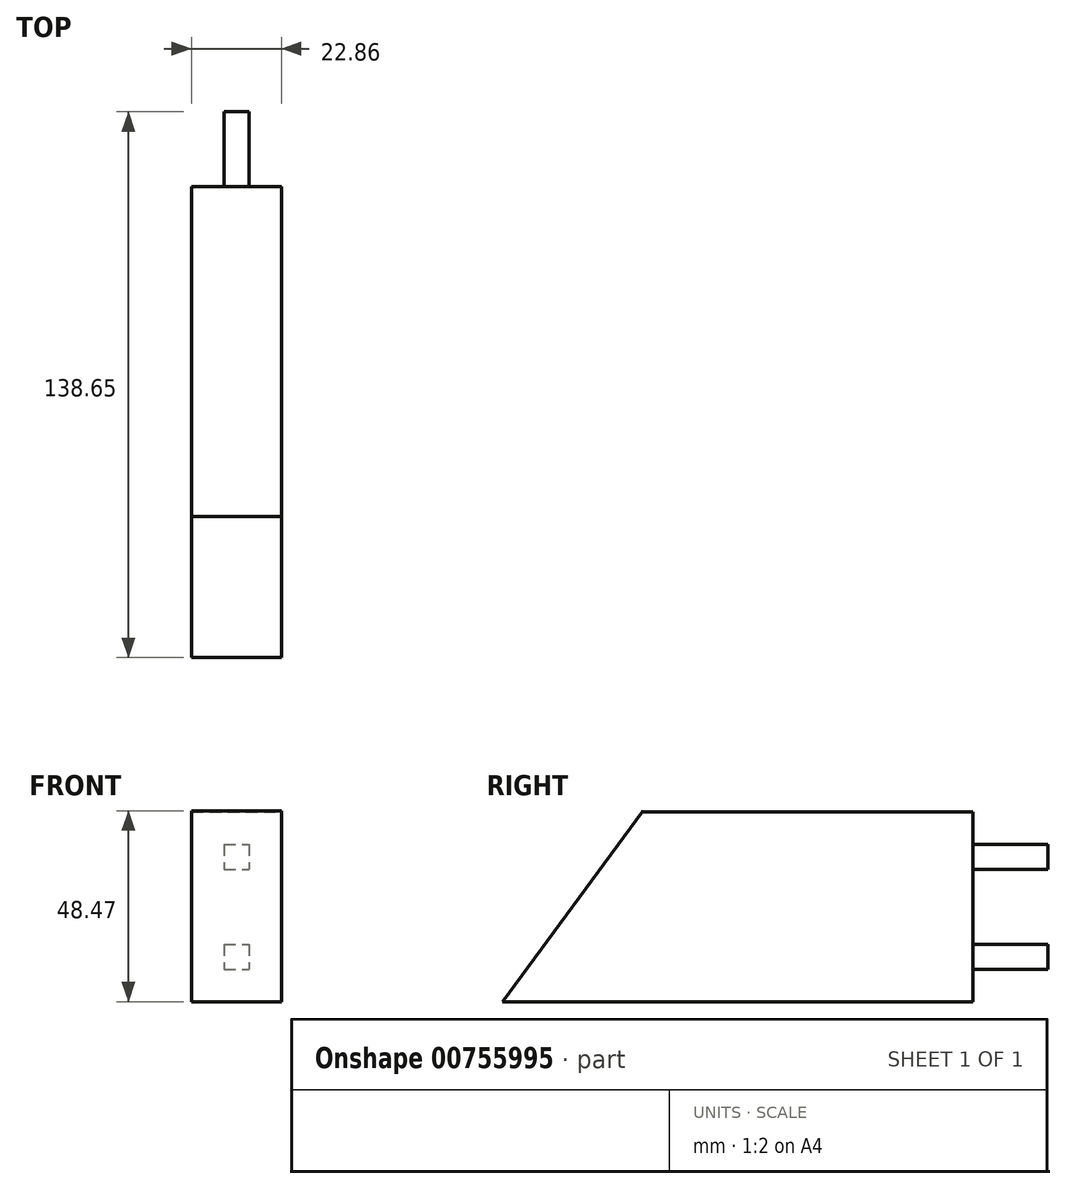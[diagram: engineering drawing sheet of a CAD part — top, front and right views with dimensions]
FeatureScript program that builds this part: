
annotation { "Feature Type Name" : "Feature", "Feature Type Description" : "" }
export const myFeature = defineFeature(function(context is Context, id is Id, definition is map)
    precondition{}
    {
        {
            var Q0;
            Q0=qCreatedBy(makeId("Top.planeOp"),FACE);
            var sketch = newSketch(context, id + "F0", { "sketchPlane" : qUnion([Q0])});
            skLineSegment(sketch, "E0.bottom", {"start": v(0, 0) * mm, "end": v(22.86, 0) * mm});
            skLineSegment(sketch, "E0.top", {"start": v(0, 83.82) * mm, "end": v(22.86, 83.82) * mm});
            skLineSegment(sketch, "E0.left", {"start": v(0, 0) * mm, "end": v(0, 83.82) * mm});
            skLineSegment(sketch, "E0.right", {"start": v(22.86, 0) * mm, "end": v(22.86, 83.82) * mm});
            skSolve(sketch);
        }
        {
            var Q0;
            Q0 = qSketchRegion(id + "F0", true);
            extrude(context, id + "F1", {"entities" : qUnion([Q0]), "depth" : 48.26 * mm, "offsetDistance" : 25.4 * mm});
        }
        {
            var Q0;
            Q0=makeQuery(id+"F1.opExtrude","SWEPT_FACE",FACE,{"disambiguationData":[OSD([sQuery(id+"F0.wireOp",EDGE,"E0.top")])]});
            var sketch = newSketch(context, id + "F2", { "sketchPlane" : qUnion([Q0])});
            skLineSegment(sketch, "E1", {"start": v(-11.43, 48.26) * mm, "end": v(-11.43, 36.83) * mm});
            skLineSegment(sketch, "E2", {"start": v(-11.43, 36.83) * mm, "end": v(-11.43, 11.43) * mm});
            skPoint(sketch, "E2.endSnap0", {"position": v(-11.43, 0) * mm});
            skLineSegment(sketch, "E3.bottom", {"start": v(-8.25, 40) * mm, "end": v(-14.6, 40) * mm});
            skLineSegment(sketch, "E3.top", {"start": v(-8.25, 33.66) * mm, "end": v(-14.6, 33.66) * mm});
            skLineSegment(sketch, "E3.left", {"start": v(-8.25, 40) * mm, "end": v(-8.25, 33.66) * mm});
            skLineSegment(sketch, "E3.right", {"start": v(-14.6, 40) * mm, "end": v(-14.6, 33.66) * mm});
            skPoint(sketch, "E3.middle", {"position": v(-11.43, 36.83) * mm});
            skLineSegment(sketch, "E4.bottom", {"start": v(-8.25, 14.6) * mm, "end": v(-14.6, 14.6) * mm});
            skLineSegment(sketch, "E4.top", {"start": v(-8.25, 8.25) * mm, "end": v(-14.6, 8.25) * mm});
            skLineSegment(sketch, "E4.left", {"start": v(-8.25, 14.6) * mm, "end": v(-8.25, 8.25) * mm});
            skLineSegment(sketch, "E4.right", {"start": v(-14.6, 14.6) * mm, "end": v(-14.6, 8.25) * mm});
            skPoint(sketch, "E4.middle", {"position": v(-11.43, 11.43) * mm});
            skSolve(sketch);
        }
        {
            var Q0;
            Q0 = qSketchRegion(id + "F2", true);
            extrude(context, id + "F3", {"entities" : qUnion([Q0]), "operationType" : NewBodyOperationType.ADD, "depth" : 19.05 * mm, "offsetDistance" : 25.4 * mm});
        }
        {
            var Q0;
            Q0=qCreatedBy(makeId("Right.planeOp"),FACE);
            var sketch = newSketch(context, id + "F4", { "sketchPlane" : qUnion([Q0])});
            skLineSegment(sketch, "E5", {"start": v(0, 0) * mm, "end": v(-35.78, 0) * mm});
            skLineSegment(sketch, "E6", {"start": v(-35.78, 0) * mm, "end": v(0, 48.47) * mm});
            skLineSegment(sketch, "E7", {"start": v(0, 48.47) * mm, "end": v(0, 0) * mm});
            skSolve(sketch);
        }
        {
            var Q0;
            Q0 = qSketchRegion(id + "F4", true);
            extrude(context, id + "F5", {"entities" : qUnion([Q0]), "operationType" : NewBodyOperationType.ADD, "depth" : 22.86 * mm, "offsetDistance" : 25.4 * mm});
        }
    });
